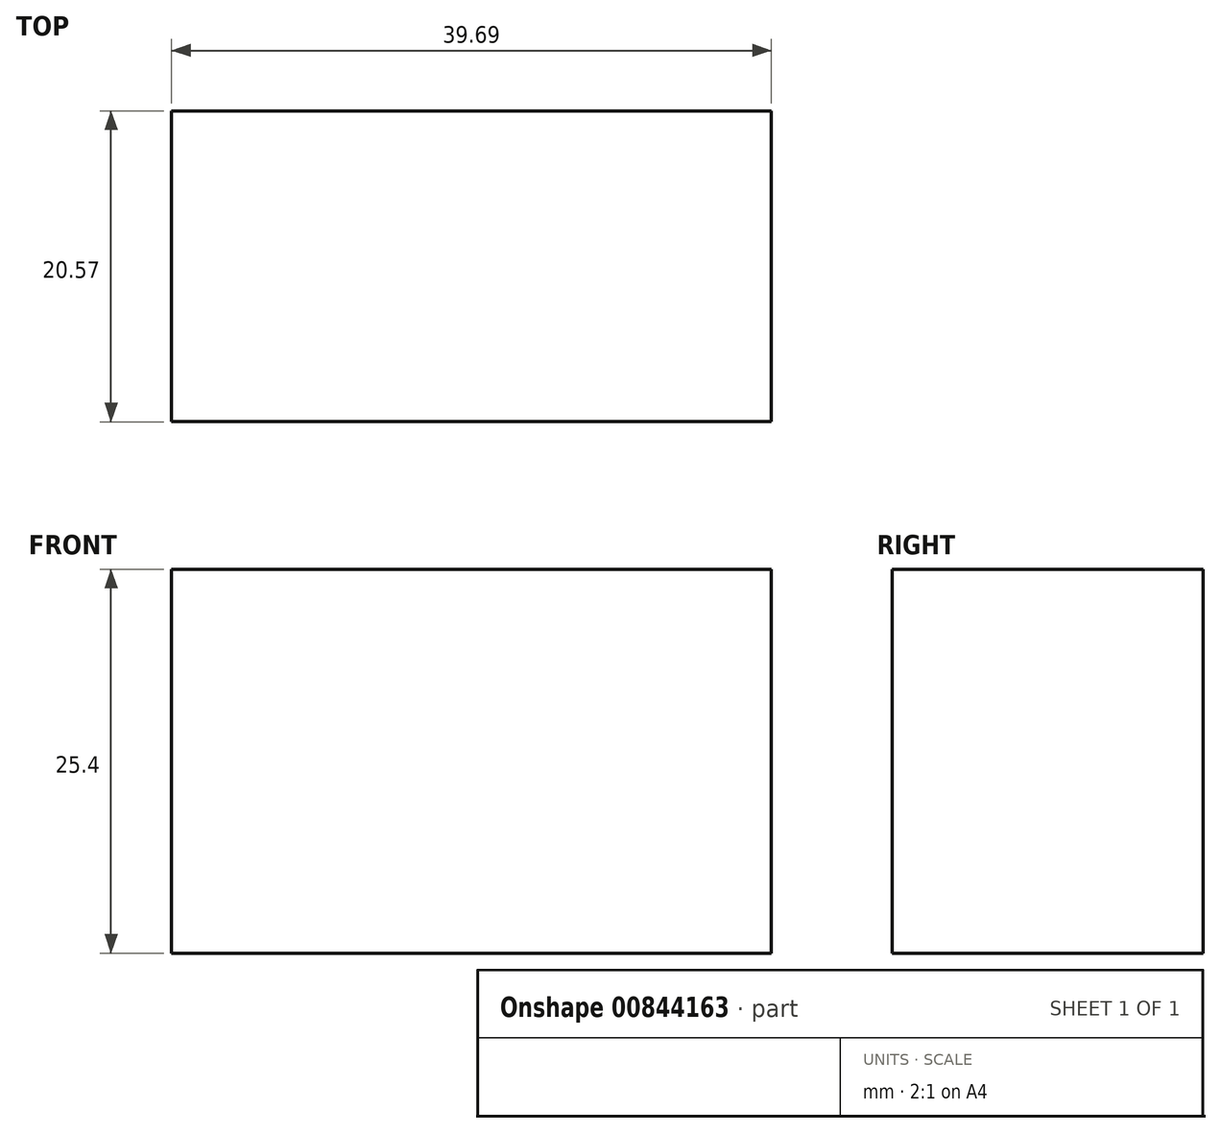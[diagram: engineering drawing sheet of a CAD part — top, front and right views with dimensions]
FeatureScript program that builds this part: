
annotation { "Feature Type Name" : "Feature", "Feature Type Description" : "" }
export const myFeature = defineFeature(function(context is Context, id is Id, definition is map)
    precondition{}
    {
        {
            var Q0;
            Q0=qCreatedBy(makeId("Top.planeOp"),FACE);
            var sketch = newSketch(context, id + "F0", { "sketchPlane" : qUnion([Q0])});
            skLineSegment(sketch, "E0.bottom", {"start": v(-39.7, -20.57) * mm, "end": v(0, -20.57) * mm});
            skLineSegment(sketch, "E0.top", {"start": v(-39.7, 0) * mm, "end": v(0, 0) * mm});
            skLineSegment(sketch, "E0.left", {"start": v(-39.7, -20.57) * mm, "end": v(-39.7, 0) * mm});
            skLineSegment(sketch, "E0.right", {"start": v(0, -20.57) * mm, "end": v(0, 0) * mm});
            skSolve(sketch);
        }
        {
            var Q0;
            Q0=makeQuery(id+"F0.imprint","IMPRINT",FACE,{"disambiguationData":[TD([[makeQuery(id+"F0.imprint","IMPRINT",EDGE,{"derivedFrom":sQuery(id+"F0.wireOp",EDGE,"E0.bottom")}),1.0]])]});
            extrude(context, id + "F1", {"entities" : qUnion([Q0]), "depth" : 25.4 * mm, "offsetDistance" : 25.4 * mm});
        }
    });
